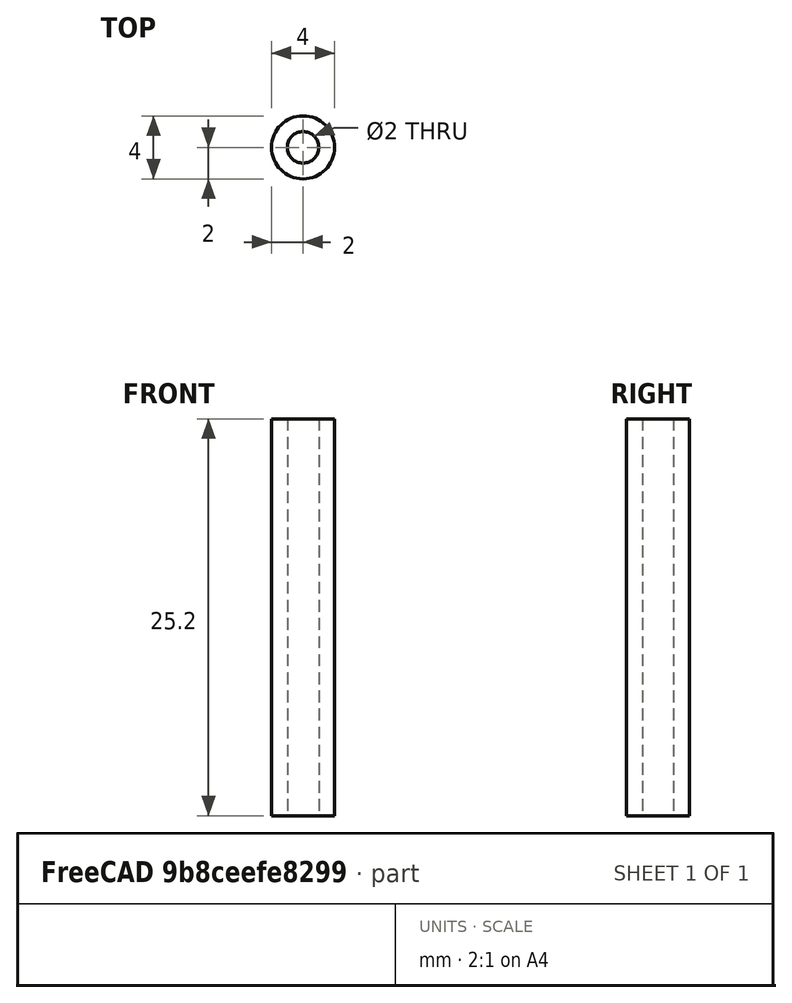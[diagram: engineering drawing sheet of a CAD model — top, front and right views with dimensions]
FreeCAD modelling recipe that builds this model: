
FCSTD DOCUMENT  (FreeCAD 0.14R3702 (Git))
Label: hotend-ptfe-tube
License: CC-BY 3.0
LicenseURL: http://creativecommons.org/licenses/by/3.0/
objects: Sketcher::SketchObject×1, PartDesign::Revolution×1, Part::Feature×1
note: 4 computed .brp shape members not serialized (recipe doc carries the construction recipe); baked Part::Feature solids carry a one-line shape summary decoded from their .brp

FEATURE [Sketcher::SketchObject] Sketch  label="main-body-sketch"
  Placement = pos=(0,0,0) rot=(-1,0,0;4.71239rad)
  sketch-geometry (4):
    g0: LineSegment StartX=-2 StartY=25.2 StartZ=0 EndX=-1 EndY=25.2 EndZ=0
    g1: LineSegment StartX=-1 StartY=25.2 StartZ=0 EndX=-1 EndY=0 EndZ=0
    g2: LineSegment StartX=-1 StartY=0 StartZ=0 EndX=-2 EndY=0 EndZ=0
    g3: LineSegment StartX=-2 StartY=0 StartZ=0 EndX=-2 EndY=25.2 EndZ=0
  constraints (12):
    c: Coincident(g0,g1)
    c: Coincident(g1,g2)
    c: Coincident(g2,g3)
    c: Coincident(g3,g0)
    c: Horizontal(g0)
    c: Horizontal(g2)
    c: Vertical(g1)
    c: Vertical(g3)
    c: PointOnObject(g1,g-1)
    c: DistanceX(g-1,g1) = -1
    c: DistanceX(g-1,g2) = -2
    c: DistanceY(g3) = 25.2
FEATURE [PartDesign::Revolution] Revolution  label="main-body"
  Angle = 360
  Axis = (0,0,1)
  Base = (0,0,0)
  Placement = pos=(0,0,0) rot=(-1,0,0;4.71239rad)
  ReferenceAxis = -> Sketch [V_Axis]
  Sketch = -> Sketch
FEATURE [Part::Feature] Revolution001  label="extruder-ptfe-tube-final"
  Placement = pos=(0,0,0) rot=(1,0,0;1.5708rad)
  shape: bbox 4 x 4 x 25.2 mm, 4 faces (baked)
